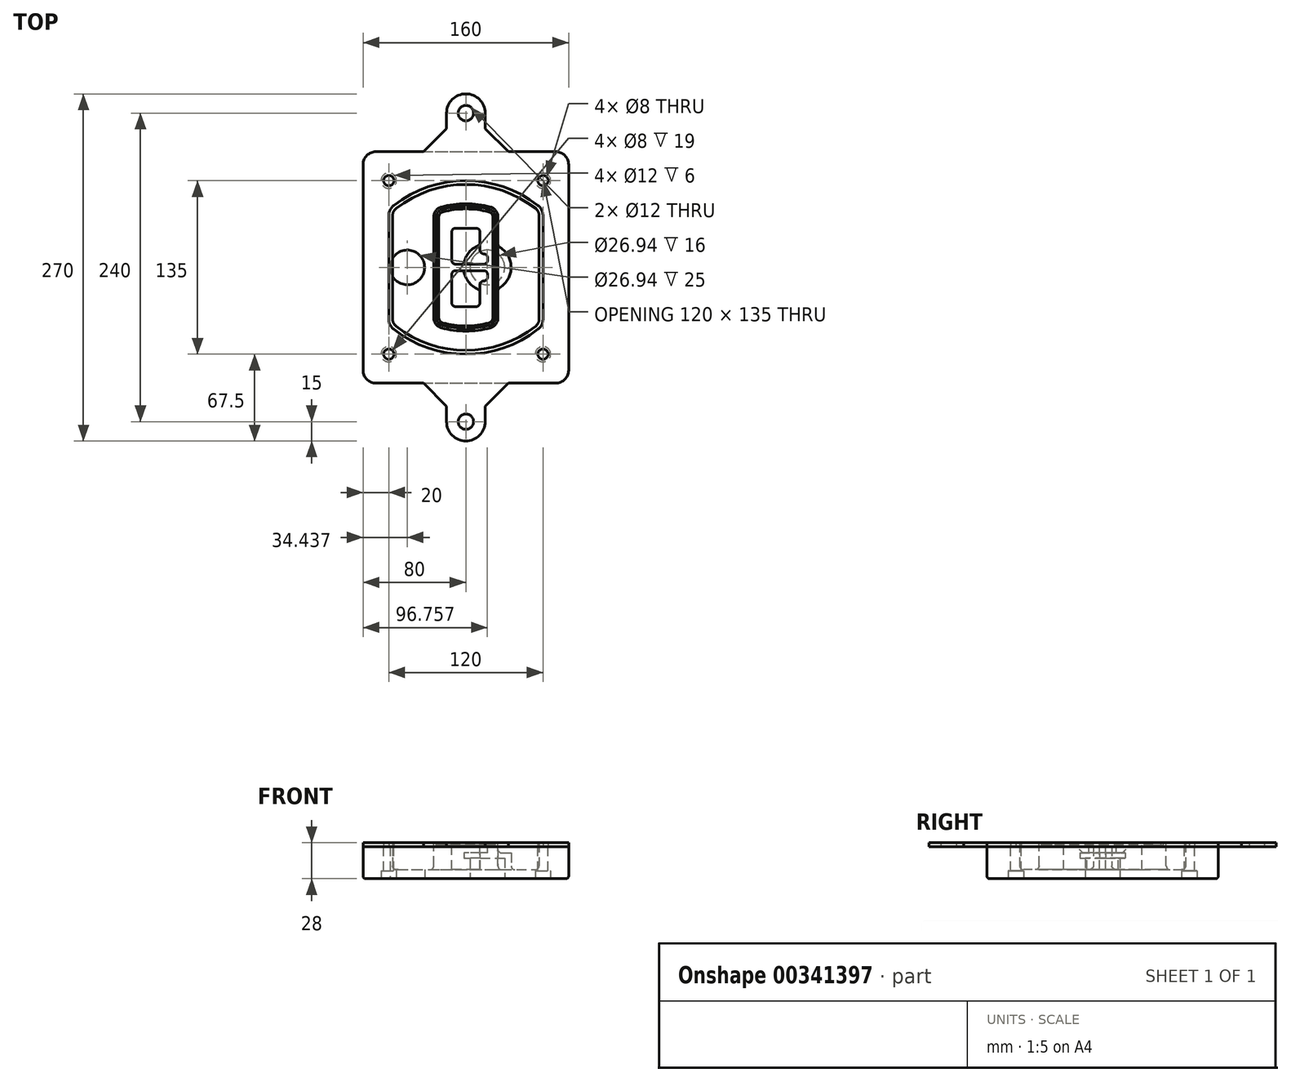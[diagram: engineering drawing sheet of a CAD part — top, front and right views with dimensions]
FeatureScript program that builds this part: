
annotation { "Feature Type Name" : "Feature", "Feature Type Description" : "" }
export const myFeature = defineFeature(function(context is Context, id is Id, definition is map)
    precondition{}
    {
        {
            var Q0;
            Q0=qCreatedBy(makeId("Top.planeOp"),FACE);
            var sketch = newSketch(context, id + "F0", { "sketchPlane" : qUnion([Q0])});
            skPoint(sketch, "E0.rect.middle", {"position": v(0, 0) * mm});
            skLineSegment(sketch, "E1.bottom", {"start": v(-70, -90) * mm, "end": v(70, -90) * mm});
            skLineSegment(sketch, "E1.top", {"start": v(-70, 90) * mm, "end": v(70, 90) * mm});
            skLineSegment(sketch, "E1.left", {"start": v(-80, -80) * mm, "end": v(-80, 80) * mm});
            skLineSegment(sketch, "E1.right", {"start": v(80, -80) * mm, "end": v(80, 80) * mm});
            skLineSegment(sketch, "E2", {"start": v(-80, 90) * mm, "end": v(80, -90) * mm, "construction": true});
            skLineSegment(sketch, "E3", {"start": v(80, 90) * mm, "end": v(-80, -90) * mm, "construction": true});
            skCircle(sketch, "E4", {"center": v(-60, 67.5) * mm, "radius": 4 * mm});
            skCircle(sketch, "E5", {"center": v(60, 67.5) * mm, "radius": 4 * mm});
            skCircle(sketch, "E6", {"center": v(60, -67.5) * mm, "radius": 4 * mm});
            skCircle(sketch, "E7", {"center": v(-60, -67.5) * mm, "radius": 4 * mm});
            skLineSegment(sketch, "E8", {"start": v(-60, 67.5) * mm, "end": v(60, 67.5) * mm, "construction": true});
            skLineSegment(sketch, "E9", {"start": v(60, 67.5) * mm, "end": v(60, -67.5) * mm, "construction": true});
            skLineSegment(sketch, "E10", {"start": v(60, -67.5) * mm, "end": v(-60, -67.5) * mm, "construction": true});
            skLineSegment(sketch, "E11", {"start": v(-60, -67.5) * mm, "end": v(-60, 67.5) * mm, "construction": true});
            skLineSegment(sketch, "E12", {"start": v(-60, 40.3) * mm, "end": v(-60, -40.3) * mm});
            skLineSegment(sketch, "E13", {"start": v(60, 40.3) * mm, "end": v(60, -40.3) * mm});
            skArc(sketch, "E14", {"start": v(56.15, 48.18) * mm, "mid": v(0, 67.5) * mm, "end": v(-56.15, 48.18) * mm});
            skArc(sketch, "E15", {"start": v(-56.15, -48.18) * mm, "mid": v(0, -67.5) * mm, "end": v(56.15, -48.18) * mm});
            skLineSegment(sketch, "E16", {"start": v(-60, 0) * mm, "end": v(60, 0) * mm, "construction": true});
            skPoint(sketch, "E17.visualSharp", {"position": v(-60, -45) * mm});
            skArc(sketch, "E17.filletArc", {"start": v(-60, -40.3) * mm, "mid": v(-58.99, -44.68) * mm, "end": v(-56.15, -48.18) * mm});
            skPoint(sketch, "E18.visualSharp", {"position": v(-60, 45) * mm});
            skArc(sketch, "E18.filletArc", {"start": v(-56.15, 48.18) * mm, "mid": v(-58.99, 44.68) * mm, "end": v(-60, 40.3) * mm});
            skPoint(sketch, "E19.visualSharp", {"position": v(60, 45) * mm});
            skArc(sketch, "E19.filletArc", {"start": v(60, 40.3) * mm, "mid": v(58.99, 44.68) * mm, "end": v(56.15, 48.18) * mm});
            skPoint(sketch, "E20.visualSharp", {"position": v(60, -45) * mm});
            skArc(sketch, "E20.filletArc", {"start": v(56.15, -48.18) * mm, "mid": v(58.99, -44.68) * mm, "end": v(60, -40.3) * mm});
            skPoint(sketch, "E21.visualSharp", {"position": v(-80, 90) * mm});
            skArc(sketch, "E21.filletArc", {"start": v(-70, 90) * mm, "mid": v(-77.07, 87.07) * mm, "end": v(-80, 80) * mm});
            skPoint(sketch, "E22.visualSharp", {"position": v(80, 90) * mm});
            skArc(sketch, "E22.filletArc", {"start": v(80, 80) * mm, "mid": v(77.07, 87.07) * mm, "end": v(70, 90) * mm});
            skPoint(sketch, "E23.visualSharp", {"position": v(80, -90) * mm});
            skArc(sketch, "E23.filletArc", {"start": v(70, -90) * mm, "mid": v(77.07, -87.07) * mm, "end": v(80, -80) * mm});
            skPoint(sketch, "E24.visualSharp", {"position": v(-80, -90) * mm});
            skArc(sketch, "E24.filletArc", {"start": v(-80, -80) * mm, "mid": v(-77.07, -87.07) * mm, "end": v(-70, -90) * mm});
            skArc(sketch, "E25.0", {"start": v(57, 40.3) * mm, "mid": v(56.3, 43.36) * mm, "end": v(54.3, 45.81) * mm});
            skLineSegment(sketch, "E25.1", {"start": v(57, 40.3) * mm, "end": v(57, -40.3) * mm});
            skArc(sketch, "E25.2", {"start": v(54.3, -45.81) * mm, "mid": v(56.3, -43.36) * mm, "end": v(57, -40.3) * mm});
            skArc(sketch, "E25.3", {"start": v(-54.3, -45.81) * mm, "mid": v(0, -64.5) * mm, "end": v(54.3, -45.81) * mm});
            skArc(sketch, "E25.4", {"start": v(-57, -40.3) * mm, "mid": v(-56.3, -43.36) * mm, "end": v(-54.3, -45.81) * mm});
            skArc(sketch, "E25.5", {"start": v(54.3, 45.81) * mm, "mid": v(0, 64.5) * mm, "end": v(-54.3, 45.81) * mm});
            skLineSegment(sketch, "E25.6", {"start": v(-57, 40.3) * mm, "end": v(-57, -40.3) * mm});
            skArc(sketch, "E25.7", {"start": v(-54.3, 45.81) * mm, "mid": v(-56.3, 43.36) * mm, "end": v(-57, 40.3) * mm});
            skArc(sketch, "E26.0", {"start": v(-58.62, 51.33) * mm, "mid": v(-62.58, 46.43) * mm, "end": v(-64, 40.3) * mm});
            skArc(sketch, "E26.1", {"start": v(58.62, 51.33) * mm, "mid": v(0, 71.5) * mm, "end": v(-58.62, 51.33) * mm});
            skArc(sketch, "E26.2", {"start": v(64, 40.3) * mm, "mid": v(62.58, 46.43) * mm, "end": v(58.62, 51.33) * mm});
            skLineSegment(sketch, "E26.3", {"start": v(64, 40.3) * mm, "end": v(64, -40.3) * mm});
            skArc(sketch, "E26.4", {"start": v(58.62, -51.33) * mm, "mid": v(62.58, -46.43) * mm, "end": v(64, -40.3) * mm});
            skLineSegment(sketch, "E26.5", {"start": v(-64, 40.3) * mm, "end": v(-64, -40.3) * mm});
            skArc(sketch, "E26.6", {"start": v(-58.62, -51.33) * mm, "mid": v(0, -71.5) * mm, "end": v(58.62, -51.33) * mm});
            skArc(sketch, "E26.7", {"start": v(-64, -40.3) * mm, "mid": v(-62.58, -46.43) * mm, "end": v(-58.62, -51.33) * mm});
            skSolve(sketch);
        }
        {
            var Q0;
            Q0=makeQuery(id+"F0.imprint","IMPRINT",FACE,{"disambiguationData":[TD([[makeQuery(id+"F0.imprint","IMPRINT",EDGE,{"derivedFrom":sQuery(id+"F0.wireOp",EDGE,"E1.bottom")}),1.0]])]});
            var Q1;
            Q1=makeQuery(id+"F0.imprint","IMPRINT",FACE,{"disambiguationData":[TD([[makeQuery(id+"F0.imprint","IMPRINT",EDGE,{"derivedFrom":sQuery(id+"F0.wireOp",EDGE,"E12")}),1.0]])]});
            var Q2;
            Q2=makeQuery(id+"F0.imprint","IMPRINT",FACE,{"disambiguationData":[TD([[makeQuery(id+"F0.imprint","IMPRINT",EDGE,{"derivedFrom":sQuery(id+"F0.wireOp",EDGE,"E25.0")}),1.0]])]});
            var Q3;
            Q3=makeQuery(id+"F0.imprint","IMPRINT",FACE,{"disambiguationData":[TD([[makeQuery(id+"F0.imprint","IMPRINT",EDGE,{"derivedFrom":sQuery(id+"F0.wireOp",EDGE,"E12")}),-1.0]])]});
            extrude(context, id + "F1", {"entities" : qUnion([Q0, Q1, Q2, Q3]), "oppositeDirection" : true, "depth" : 25 * mm});
        }
        {
            var Q0;
            Q0=makeQuery(id+"F0.imprint","IMPRINT",FACE,{"disambiguationData":[TD([[makeQuery(id+"F0.imprint","IMPRINT",EDGE,{"derivedFrom":sQuery(id+"F0.wireOp",EDGE,"E12")}),1.0]])]});
            extrude(context, id + "F2", {"entities" : qUnion([Q0]), "operationType" : NewBodyOperationType.ADD, "depth" : 3 * mm});
        }
        {
            var Q0;
            Q0=makeQuery(id+"F0.imprint","IMPRINT",FACE,{"disambiguationData":[TD([[makeQuery(id+"F0.imprint","IMPRINT",EDGE,{"derivedFrom":sQuery(id+"F0.wireOp",EDGE,"E25.0")}),1.0]])]});
            extrude(context, id + "F3", {"entities" : qUnion([Q0]), "operationType" : NewBodyOperationType.REMOVE, "oppositeDirection" : true, "depth" : 18 * mm});
        }
        {
            var Q0;
            Q0=makeQuery(id+"F2.opExtrude","CAP_FACE",FACE,{"disambiguationData":[OSD([sQuery(id+"F0.wireOp",EDGE,"E12"),sQuery(id+"F0.wireOp",EDGE,"E13"),sQuery(id+"F0.wireOp",EDGE,"E14"),sQuery(id+"F0.wireOp",EDGE,"E15"),sQuery(id+"F0.wireOp",EDGE,"E17.filletArc"),sQuery(id+"F0.wireOp",EDGE,"E18.filletArc"),sQuery(id+"F0.wireOp",EDGE,"E19.filletArc"),sQuery(id+"F0.wireOp",EDGE,"E20.filletArc"),sQuery(id+"F0.wireOp",EDGE,"E25.0"),sQuery(id+"F0.wireOp",EDGE,"E25.1"),sQuery(id+"F0.wireOp",EDGE,"E25.2"),sQuery(id+"F0.wireOp",EDGE,"E25.3"),sQuery(id+"F0.wireOp",EDGE,"E25.4"),sQuery(id+"F0.wireOp",EDGE,"E25.5"),sQuery(id+"F0.wireOp",EDGE,"E25.6"),sQuery(id+"F0.wireOp",EDGE,"E25.7")])],"isStart":false});
            var sketch = newSketch(context, id + "F4", { "sketchPlane" : qUnion([Q0])});
            skArc(sketch, "E27.0", {"start": v(-19.08, -46.97) * mm, "mid": v(0, -49.5) * mm, "end": v(19.08, -46.97) * mm});
            skArc(sketch, "E28.0", {"start": v(19.08, 46.97) * mm, "mid": v(0, 49.5) * mm, "end": v(-19.08, 46.97) * mm});
            skLineSegment(sketch, "E29", {"start": v(-25, 39.25) * mm, "end": v(-25, -39.25) * mm});
            skLineSegment(sketch, "E30", {"start": v(25, 39.25) * mm, "end": v(25, -39.25) * mm});
            skLineSegment(sketch, "E31", {"start": v(-25, 45.1) * mm, "end": v(25, 45.1) * mm, "construction": true});
            skLineSegment(sketch, "E32", {"start": v(-25, -45.1) * mm, "end": v(25, -45.1) * mm, "construction": true});
            skPoint(sketch, "E33.visualSharp", {"position": v(-25, 45.1) * mm});
            skArc(sketch, "E33.filletArc", {"start": v(-19.08, 46.97) * mm, "mid": v(-23.35, 44.11) * mm, "end": v(-25, 39.25) * mm});
            skPoint(sketch, "E34.visualSharp", {"position": v(25, 45.1) * mm});
            skArc(sketch, "E34.filletArc", {"start": v(25, 39.25) * mm, "mid": v(23.35, 44.11) * mm, "end": v(19.08, 46.97) * mm});
            skPoint(sketch, "E35.visualSharp", {"position": v(25, -45.1) * mm});
            skArc(sketch, "E35.filletArc", {"start": v(19.08, -46.97) * mm, "mid": v(23.35, -44.11) * mm, "end": v(25, -39.25) * mm});
            skPoint(sketch, "E36.visualSharp", {"position": v(-25, -45.1) * mm});
            skArc(sketch, "E36.filletArc", {"start": v(-25, -39.25) * mm, "mid": v(-23.35, -44.11) * mm, "end": v(-19.08, -46.97) * mm});
            skArc(sketch, "E37.0", {"start": v(54.3, 45.81) * mm, "mid": v(0, 64.5) * mm, "end": v(-54.3, 45.81) * mm});
            skArc(sketch, "E37.1", {"start": v(-54.3, 45.81) * mm, "mid": v(-56.3, 43.36) * mm, "end": v(-57, 40.3) * mm});
            skLineSegment(sketch, "E37.2", {"start": v(-57, 40.3) * mm, "end": v(-57, -40.3) * mm});
            skArc(sketch, "E37.3", {"start": v(-57, -40.3) * mm, "mid": v(-56.3, -43.36) * mm, "end": v(-54.3, -45.81) * mm});
            skArc(sketch, "E37.4", {"start": v(-54.3, -45.81) * mm, "mid": v(0, -64.5) * mm, "end": v(54.3, -45.81) * mm});
            skArc(sketch, "E37.5", {"start": v(54.3, -45.81) * mm, "mid": v(56.3, -43.36) * mm, "end": v(57, -40.3) * mm});
            skLineSegment(sketch, "E37.6", {"start": v(57, 40.3) * mm, "end": v(57, -40.3) * mm});
            skArc(sketch, "E37.7", {"start": v(57, 40.3) * mm, "mid": v(56.3, 43.36) * mm, "end": v(54.3, 45.81) * mm});
            skLineSegment(sketch, "E38.0", {"start": v(23, 39.25) * mm, "end": v(23, -39.25) * mm});
            skArc(sketch, "E38.1", {"start": v(18.56, -45.04) * mm, "mid": v(21.76, -42.9) * mm, "end": v(23, -39.25) * mm});
            skArc(sketch, "E38.2", {"start": v(-18.56, -45.04) * mm, "mid": v(0, -47.5) * mm, "end": v(18.56, -45.04) * mm});
            skArc(sketch, "E38.3", {"start": v(-23, -39.25) * mm, "mid": v(-21.76, -42.9) * mm, "end": v(-18.56, -45.04) * mm});
            skLineSegment(sketch, "E38.4", {"start": v(-23, 39.25) * mm, "end": v(-23, -39.25) * mm});
            skArc(sketch, "E38.5", {"start": v(23, 39.25) * mm, "mid": v(21.76, 42.9) * mm, "end": v(18.56, 45.04) * mm});
            skArc(sketch, "E38.6", {"start": v(-18.56, 45.04) * mm, "mid": v(-21.76, 42.9) * mm, "end": v(-23, 39.25) * mm});
            skArc(sketch, "E38.7", {"start": v(18.56, 45.04) * mm, "mid": v(0, 47.5) * mm, "end": v(-18.56, 45.04) * mm});
            skArc(sketch, "E39.0", {"start": v(21, 39.25) * mm, "mid": v(20.18, 41.68) * mm, "end": v(18.04, 43.1) * mm});
            skLineSegment(sketch, "E39.1", {"start": v(21, 39.25) * mm, "end": v(21, -39.25) * mm});
            skArc(sketch, "E39.2", {"start": v(18.04, -43.1) * mm, "mid": v(20.18, -41.68) * mm, "end": v(21, -39.25) * mm});
            skArc(sketch, "E39.3", {"start": v(-18.04, -43.1) * mm, "mid": v(0, -45.5) * mm, "end": v(18.04, -43.1) * mm});
            skArc(sketch, "E39.4", {"start": v(-21, -39.25) * mm, "mid": v(-20.18, -41.68) * mm, "end": v(-18.04, -43.1) * mm});
            skArc(sketch, "E39.5", {"start": v(18.04, 43.1) * mm, "mid": v(0, 45.5) * mm, "end": v(-18.04, 43.1) * mm});
            skLineSegment(sketch, "E39.6", {"start": v(-21, 39.25) * mm, "end": v(-21, -39.25) * mm});
            skArc(sketch, "E39.7", {"start": v(-18.04, 43.1) * mm, "mid": v(-20.18, 41.68) * mm, "end": v(-21, 39.25) * mm});
            skLineSegment(sketch, "E40", {"start": v(-25, 0) * mm, "end": v(25, 0) * mm, "construction": true});
            skLineSegment(sketch, "E41", {"start": v(-11, 5.5) * mm, "end": v(-11, 27.5) * mm});
            skLineSegment(sketch, "E42", {"start": v(-8, 30.5) * mm, "end": v(8, 30.5) * mm});
            skLineSegment(sketch, "E43", {"start": v(11, 27.5) * mm, "end": v(11, 13.5) * mm});
            skLineSegment(sketch, "E44", {"start": v(14, 10.5) * mm, "end": v(14, 10.5) * mm});
            skLineSegment(sketch, "E45", {"start": v(17, 7.5) * mm, "end": v(17, 5.5) * mm});
            skLineSegment(sketch, "E46", {"start": v(14, 2.5) * mm, "end": v(-8, 2.5) * mm});
            skPoint(sketch, "E47.visualSharp", {"position": v(-11, 30.5) * mm});
            skArc(sketch, "E47.filletArc", {"start": v(-8, 30.5) * mm, "mid": v(-10.12, 29.62) * mm, "end": v(-11, 27.5) * mm});
            skPoint(sketch, "E48.visualSharp", {"position": v(11, 30.5) * mm});
            skArc(sketch, "E48.filletArc", {"start": v(11, 27.5) * mm, "mid": v(10.12, 29.62) * mm, "end": v(8, 30.5) * mm});
            skPoint(sketch, "E49.visualSharp", {"position": v(11, 10.5) * mm});
            skArc(sketch, "E49.filletArc", {"start": v(11, 13.5) * mm, "mid": v(11.88, 11.38) * mm, "end": v(14, 10.5) * mm});
            skPoint(sketch, "E50.visualSharp", {"position": v(17, 10.5) * mm});
            skArc(sketch, "E50.filletArc", {"start": v(17, 7.5) * mm, "mid": v(16.12, 9.62) * mm, "end": v(14, 10.5) * mm});
            skPoint(sketch, "E51.visualSharp", {"position": v(17, 2.5) * mm});
            skArc(sketch, "E51.filletArc", {"start": v(14, 2.5) * mm, "mid": v(16.12, 3.38) * mm, "end": v(17, 5.5) * mm});
            skPoint(sketch, "E52.visualSharp", {"position": v(-11, 2.5) * mm});
            skArc(sketch, "E52.filletArc", {"start": v(-11, 5.5) * mm, "mid": v(-10.12, 3.38) * mm, "end": v(-8, 2.5) * mm});
            skLineSegment(sketch, "E53.0.MirrorCS", {"start": v(14, -2.5) * mm, "end": v(-8, -2.5) * mm});
            skArc(sketch, "E54.0.MirrorCS", {"start": v(-11, -5.5) * mm, "mid": v(-10.12, -3.38) * mm, "end": v(-8, -2.5) * mm});
            skLineSegment(sketch, "E55.0.MirrorCS", {"start": v(-11, -5.5) * mm, "end": v(-11, -27.5) * mm});
            skArc(sketch, "E56.0.MirrorCS", {"start": v(-8, -30.5) * mm, "mid": v(-10.12, -29.62) * mm, "end": v(-11, -27.5) * mm});
            skLineSegment(sketch, "E57.0.MirrorCS", {"start": v(-8, -30.5) * mm, "end": v(8, -30.5) * mm});
            skArc(sketch, "E58.0.MirrorCS", {"start": v(11, -27.5) * mm, "mid": v(10.12, -29.62) * mm, "end": v(8, -30.5) * mm});
            skLineSegment(sketch, "E59.0.MirrorCS", {"start": v(11, -27.5) * mm, "end": v(11, -13.5) * mm});
            skArc(sketch, "E60.0.MirrorCS", {"start": v(11, -13.5) * mm, "mid": v(11.88, -11.38) * mm, "end": v(14, -10.5) * mm});
            skArc(sketch, "E61.0.MirrorCS", {"start": v(17, -7.5) * mm, "mid": v(16.12, -9.62) * mm, "end": v(14, -10.5) * mm});
            skLineSegment(sketch, "E62.0.MirrorCS", {"start": v(17, -7.5) * mm, "end": v(17, -5.5) * mm});
            skArc(sketch, "E63.0.MirrorCS", {"start": v(14, -2.5) * mm, "mid": v(16.12, -3.38) * mm, "end": v(17, -5.5) * mm});
            skSolve(sketch);
        }
        {
            var Q0;
            Q0=makeQuery(id+"F4.imprint","IMPRINT",FACE,{"disambiguationData":[TD([[makeQuery(id+"F4.imprint","IMPRINT",EDGE,{"derivedFrom":sQuery(id+"F4.wireOp",EDGE,"E27.0")}),1.0]])]});
            var Q1;
            Q1=makeQuery(id+"F4.imprint","IMPRINT",FACE,{"disambiguationData":[TD([[makeQuery(id+"F4.imprint","IMPRINT",EDGE,{"derivedFrom":sQuery(id+"F4.wireOp",EDGE,"E38.0")}),-1.0]])]});
            var Q2;
            Q2=makeQuery(id+"F4.imprint","IMPRINT",FACE,{"disambiguationData":[TD([[makeQuery(id+"F4.imprint","IMPRINT",EDGE,{"derivedFrom":sQuery(id+"F4.wireOp",EDGE,"E39.0")}),1.0]])]});
            extrude(context, id + "F5", {"entities" : qUnion([Q0, Q1, Q2]), "operationType" : NewBodyOperationType.ADD, "endBound" : BoundingType.UP_TO_NEXT, "oppositeDirection" : true, "depth" : 25 * mm});
        }
        {
            var Q0;
            Q0=makeQuery(id+"F4.imprint","IMPRINT",FACE,{"disambiguationData":[TD([[makeQuery(id+"F4.imprint","IMPRINT",EDGE,{"derivedFrom":sQuery(id+"F4.wireOp",EDGE,"E38.0")}),-1.0]])]});
            extrude(context, id + "F6", {"entities" : qUnion([Q0]), "operationType" : NewBodyOperationType.REMOVE, "oppositeDirection" : true, "depth" : 2 * mm});
        }
        {
            var Q0;
            Q0=makeQuery(id+"F1.opExtrude","CAP_FACE",FACE,{"disambiguationData":[OSD([sQuery(id+"F0.wireOp",EDGE,"E1.bottom"),sQuery(id+"F0.wireOp",EDGE,"E1.top"),sQuery(id+"F0.wireOp",EDGE,"E1.left"),sQuery(id+"F0.wireOp",EDGE,"E1.right"),sQuery(id+"F0.wireOp",EDGE,"E4"),sQuery(id+"F0.wireOp",EDGE,"E5"),sQuery(id+"F0.wireOp",EDGE,"E6"),sQuery(id+"F0.wireOp",EDGE,"E7"),sQuery(id+"F0.wireOp",EDGE,"E21.filletArc"),sQuery(id+"F0.wireOp",EDGE,"E22.filletArc"),sQuery(id+"F0.wireOp",EDGE,"E23.filletArc"),sQuery(id+"F0.wireOp",EDGE,"E24.filletArc")])],"isStart":false});
            var sketch = newSketch(context, id + "F7", { "sketchPlane" : qUnion([Q0])});
            skCircle(sketch, "E64", {"center": v(16.76, 0) * mm, "radius": 13.47 * mm});
            skCircle(sketch, "E65", {"center": v(-45.56, 0) * mm, "radius": 13.47 * mm});
            skLineSegment(sketch, "E66", {"start": v(80, 0) * mm, "end": v(-80, 0) * mm});
            skCircle(sketch, "E67", {"center": v(16.76, 0) * mm, "radius": 18.47 * mm});
            skCircle(sketch, "E68", {"center": v(60, -67.5) * mm, "radius": 6 * mm});
            skCircle(sketch, "E69", {"center": v(-60, -67.5) * mm, "radius": 6 * mm});
            skCircle(sketch, "E70", {"center": v(-60, 67.5) * mm, "radius": 6 * mm});
            skCircle(sketch, "E71", {"center": v(60, 67.5) * mm, "radius": 6 * mm});
            skSolve(sketch);
        }
        {
            var Q0;
            {var subQ1=sQuery(id+"F7.wireOp",EDGE,"E66");var subQ4=sQuery(id+"F7.wireOp",EDGE,"E64");var subQ6=makeQuery(id+"F7.imprint","INTERSECT",VERTEX,{"disambiguationData":[OD(0.0)],"derivedFrom":[subQ4,subQ1]});Q0=makeQuery(id+"F7.imprint","IMPRINT",FACE,{"disambiguationData":[TD([[makeQuery(id+"F7.imprint","IMPRINT",EDGE,{"disambiguationData":[TD([[subQ6,-1.0]])],"derivedFrom":subQ4}),-1.0]])]});}
            var Q1;
            {var subQ0=sQuery(id+"F7.wireOp",EDGE,"E66");var subQ1=sQuery(id+"F7.wireOp",EDGE,"E64");var subQ3=makeQuery(id+"F7.imprint","INTERSECT",VERTEX,{"disambiguationData":[OD(0.0)],"derivedFrom":[subQ1,subQ0]});Q1=makeQuery(id+"F7.imprint","IMPRINT",FACE,{"disambiguationData":[TD([[makeQuery(id+"F7.imprint","IMPRINT",EDGE,{"disambiguationData":[TD([[subQ3,-1.0]])],"derivedFrom":subQ1}),1.0]])]});}
            var Q2;
            {var subQ0=sQuery(id+"F7.wireOp",EDGE,"E66");var subQ1=sQuery(id+"F7.wireOp",EDGE,"E64");var subQ3=makeQuery(id+"F7.imprint","INTERSECT",VERTEX,{"disambiguationData":[OD(0.0)],"derivedFrom":[subQ1,subQ0]});Q2=makeQuery(id+"F7.imprint","IMPRINT",FACE,{"disambiguationData":[TD([[makeQuery(id+"F7.imprint","IMPRINT",EDGE,{"disambiguationData":[TD([[subQ3,1.0]])],"derivedFrom":subQ1}),1.0]])]});}
            var Q3;
            {var subQ1=sQuery(id+"F7.wireOp",EDGE,"E66");var subQ4=sQuery(id+"F7.wireOp",EDGE,"E64");var subQ6=makeQuery(id+"F7.imprint","INTERSECT",VERTEX,{"disambiguationData":[OD(0.0)],"derivedFrom":[subQ4,subQ1]});Q3=makeQuery(id+"F7.imprint","IMPRINT",FACE,{"disambiguationData":[TD([[makeQuery(id+"F7.imprint","IMPRINT",EDGE,{"disambiguationData":[TD([[subQ6,1.0]])],"derivedFrom":subQ4}),-1.0]])]});}
            extrude(context, id + "F8", {"entities" : qUnion([Q0, Q1, Q2, Q3]), "operationType" : NewBodyOperationType.ADD, "oppositeDirection" : true, "depth" : 20 * mm});
        }
        {
            var Q0;
            {var subQ0=sQuery(id+"F7.wireOp",EDGE,"E66");var subQ1=sQuery(id+"F7.wireOp",EDGE,"E64");var subQ3=makeQuery(id+"F7.imprint","INTERSECT",VERTEX,{"disambiguationData":[OD(0.0)],"derivedFrom":[subQ1,subQ0]});Q0=makeQuery(id+"F7.imprint","IMPRINT",FACE,{"disambiguationData":[TD([[makeQuery(id+"F7.imprint","IMPRINT",EDGE,{"disambiguationData":[TD([[subQ3,-1.0]])],"derivedFrom":subQ1}),1.0]])]});}
            var Q1;
            {var subQ0=sQuery(id+"F7.wireOp",EDGE,"E66");var subQ1=sQuery(id+"F7.wireOp",EDGE,"E64");var subQ3=makeQuery(id+"F7.imprint","INTERSECT",VERTEX,{"disambiguationData":[OD(0.0)],"derivedFrom":[subQ1,subQ0]});Q1=makeQuery(id+"F7.imprint","IMPRINT",FACE,{"disambiguationData":[TD([[makeQuery(id+"F7.imprint","IMPRINT",EDGE,{"disambiguationData":[TD([[subQ3,1.0]])],"derivedFrom":subQ1}),1.0]])]});}
            extrude(context, id + "F9", {"entities" : qUnion([Q0, Q1]), "operationType" : NewBodyOperationType.REMOVE, "oppositeDirection" : true, "depth" : 16 * mm});
        }
        {
            var Q0;
            {var subQ0=sQuery(id+"F7.wireOp",EDGE,"E66");var subQ1=sQuery(id+"F7.wireOp",EDGE,"E65");var subQ3=makeQuery(id+"F7.imprint","INTERSECT",VERTEX,{"disambiguationData":[OD(0.0)],"derivedFrom":[subQ1,subQ0]});Q0=makeQuery(id+"F7.imprint","IMPRINT",FACE,{"disambiguationData":[TD([[makeQuery(id+"F7.imprint","IMPRINT",EDGE,{"disambiguationData":[TD([[subQ3,-1.0]])],"derivedFrom":subQ1}),1.0]])]});}
            var Q1;
            {var subQ0=sQuery(id+"F7.wireOp",EDGE,"E66");var subQ1=sQuery(id+"F7.wireOp",EDGE,"E65");var subQ3=makeQuery(id+"F7.imprint","INTERSECT",VERTEX,{"disambiguationData":[OD(0.0)],"derivedFrom":[subQ1,subQ0]});Q1=makeQuery(id+"F7.imprint","IMPRINT",FACE,{"disambiguationData":[TD([[makeQuery(id+"F7.imprint","IMPRINT",EDGE,{"disambiguationData":[TD([[subQ3,1.0]])],"derivedFrom":subQ1}),1.0]])]});}
            extrude(context, id + "F10", {"entities" : qUnion([Q0, Q1]), "operationType" : NewBodyOperationType.REMOVE, "oppositeDirection" : true, "depth" : 25 * mm});
        }
        {
            var Q0;
            Q0=makeQuery(id+"F7.imprint","IMPRINT",FACE,{"disambiguationData":[TD([[makeQuery(id+"F7.imprint","IMPRINT",EDGE,{"derivedFrom":sQuery(id+"F7.wireOp",EDGE,"E68")}),1.0]])]});
            var Q1;
            Q1=makeQuery(id+"F7.imprint","IMPRINT",FACE,{"disambiguationData":[TD([[makeQuery(id+"F7.imprint","IMPRINT",EDGE,{"derivedFrom":makeQuery(id+"F1.opExtrude","CAP_EDGE",EDGE,{"disambiguationData":[OSD([sQuery(id+"F0.wireOp",EDGE,"E5")])],"isStart":false})}),-1.0]])]});
            var Q2;
            Q2=makeQuery(id+"F7.imprint","IMPRINT",FACE,{"disambiguationData":[TD([[makeQuery(id+"F7.imprint","IMPRINT",EDGE,{"derivedFrom":sQuery(id+"F7.wireOp",EDGE,"E69")}),1.0]])]});
            var Q3;
            Q3=makeQuery(id+"F7.imprint","IMPRINT",FACE,{"disambiguationData":[TD([[makeQuery(id+"F7.imprint","IMPRINT",EDGE,{"derivedFrom":makeQuery(id+"F1.opExtrude","CAP_EDGE",EDGE,{"disambiguationData":[OSD([sQuery(id+"F0.wireOp",EDGE,"E4")])],"isStart":false})}),-1.0]])]});
            var Q4;
            Q4=makeQuery(id+"F7.imprint","IMPRINT",FACE,{"disambiguationData":[TD([[makeQuery(id+"F7.imprint","IMPRINT",EDGE,{"derivedFrom":sQuery(id+"F7.wireOp",EDGE,"E70")}),1.0]])]});
            var Q5;
            Q5=makeQuery(id+"F7.imprint","IMPRINT",FACE,{"disambiguationData":[TD([[makeQuery(id+"F7.imprint","IMPRINT",EDGE,{"derivedFrom":makeQuery(id+"F1.opExtrude","CAP_EDGE",EDGE,{"disambiguationData":[OSD([sQuery(id+"F0.wireOp",EDGE,"E7")])],"isStart":false})}),-1.0]])]});
            var Q6;
            Q6=makeQuery(id+"F7.imprint","IMPRINT",FACE,{"disambiguationData":[TD([[makeQuery(id+"F7.imprint","IMPRINT",EDGE,{"derivedFrom":sQuery(id+"F7.wireOp",EDGE,"E71")}),1.0]])]});
            var Q7;
            Q7=makeQuery(id+"F7.imprint","IMPRINT",FACE,{"disambiguationData":[TD([[makeQuery(id+"F7.imprint","IMPRINT",EDGE,{"derivedFrom":makeQuery(id+"F1.opExtrude","CAP_EDGE",EDGE,{"disambiguationData":[OSD([sQuery(id+"F0.wireOp",EDGE,"E6")])],"isStart":false})}),-1.0]])]});
            extrude(context, id + "F11", {"entities" : qUnion([Q0, Q1, Q2, Q3, Q4, Q5, Q6, Q7]), "operationType" : NewBodyOperationType.REMOVE, "oppositeDirection" : true, "depth" : 6 * mm});
        }
        {
            var Q0;
            Q0=makeQuery(id+"F9.boolean.opBoolean","COPY",FACE,{"derivedFrom":makeQuery(id+"F9.opExtrude","CAP_FACE",FACE,{"disambiguationData":[OSD([sQuery(id+"F7.wireOp",EDGE,"E64")])],"isStart":false})});
            var sketch = newSketch(context, id + "F12", { "sketchPlane" : qUnion([Q0])});
            skArc(sketch, "E72.0", {"start": v(11, 17.55) * mm, "mid": v(2.57, 11.82) * mm, "end": v(-1.54, 2.5) * mm});
            skArc(sketch, "E72.1", {"start": v(-1.54, -2.5) * mm, "mid": v(2.57, -11.82) * mm, "end": v(11, -17.55) * mm});
            skLineSegment(sketch, "E73", {"start": v(-1.54, -2.5) * mm, "end": v(14, -2.5) * mm});
            skLineSegment(sketch, "E74.0", {"start": v(14, 2.5) * mm, "end": v(-1.54, 2.5) * mm});
            skArc(sketch, "E74.1", {"start": v(14, 2.5) * mm, "mid": v(16.12, 3.38) * mm, "end": v(17, 5.5) * mm});
            skLineSegment(sketch, "E74.2", {"start": v(17, 7.5) * mm, "end": v(17, 5.5) * mm});
            skArc(sketch, "E74.3", {"start": v(17, 7.5) * mm, "mid": v(16.12, 9.62) * mm, "end": v(14, 10.5) * mm});
            skArc(sketch, "E74.4", {"start": v(11, 13.5) * mm, "mid": v(11.88, 11.38) * mm, "end": v(14, 10.5) * mm});
            skLineSegment(sketch, "E74.5", {"start": v(11, 17.55) * mm, "end": v(11, 13.5) * mm});
            skLineSegment(sketch, "E74.7", {"start": v(14, -2.5) * mm, "end": v(-1.54, -2.5) * mm});
            skArc(sketch, "E74.8", {"start": v(14, -2.5) * mm, "mid": v(16.12, -3.38) * mm, "end": v(17, -5.5) * mm});
            skLineSegment(sketch, "E74.9", {"start": v(17, -7.5) * mm, "end": v(17, -5.5) * mm});
            skArc(sketch, "E74.10", {"start": v(17, -7.5) * mm, "mid": v(16.12, -9.62) * mm, "end": v(14, -10.5) * mm});
            skArc(sketch, "E74.11", {"start": v(11, -13.5) * mm, "mid": v(11.88, -11.38) * mm, "end": v(14, -10.5) * mm});
            skLineSegment(sketch, "E74.12", {"start": v(11, -17.55) * mm, "end": v(11, -13.5) * mm});
            skPoint(sketch, "E75.orphan", {"position": v(11, -27.5) * mm});
            skPoint(sketch, "E76.orphan", {"position": v(-8, -2.5) * mm});
            skPoint(sketch, "E77.orphan", {"position": v(-8, 2.5) * mm});
            skPoint(sketch, "E78.orphan", {"position": v(11, 27.5) * mm});
            skSolve(sketch);
        }
        {
            var Q0;
            {var subQ7=sQuery(id+"F12.wireOp",EDGE,"E72.0");var subQ14=sQuery(id+"F12.wireOp",EDGE,"E72.1");var subQ16=sQuery(id+"F12.wireOp",EDGE,"E74.1");var subQ18=sQuery(id+"F12.wireOp",EDGE,"E74.8");Q0=qUnion([makeQuery(id+"F12.imprint","IMPRINT",FACE,{"disambiguationData":[TD([[makeQuery(id+"F12.imprint","IMPRINT",EDGE,{"derivedFrom":subQ7}),1.0]])]}),makeQuery(id+"F12.imprint","IMPRINT",FACE,{"disambiguationData":[TD([[makeQuery(id+"F12.imprint","IMPRINT",EDGE,{"derivedFrom":subQ14}),1.0]])]}),makeQuery(id+"F12.imprint","IMPRINT",FACE,{"disambiguationData":[TD([[makeQuery(id+"F12.imprint","IMPRINT",EDGE,{"derivedFrom":subQ16}),1.0]])]}),makeQuery(id+"F12.imprint","IMPRINT",FACE,{"disambiguationData":[TD([[makeQuery(id+"F12.imprint","IMPRINT",EDGE,{"derivedFrom":subQ18}),-1.0]])]})]);}
            var Q1;
            Q1=makeQuery(id+"F5.boolean.opBoolean","SPLIT",FACE,{"disambiguationData":[TD([makeQuery(id+"F5.opExtrude","SWEPT_FACE",FACE,{"disambiguationData":[OSD([sQuery(id+"F4.wireOp",EDGE,"E41")])]})])],"derivedFrom":makeQuery(id+"F3.boolean.opBoolean","COPY",FACE,{"derivedFrom":makeQuery(id+"F3.opExtrude","CAP_FACE",FACE,{"disambiguationData":[OSD([sQuery(id+"F0.wireOp",EDGE,"E25.0"),sQuery(id+"F0.wireOp",EDGE,"E25.1"),sQuery(id+"F0.wireOp",EDGE,"E25.2"),sQuery(id+"F0.wireOp",EDGE,"E25.3"),sQuery(id+"F0.wireOp",EDGE,"E25.4"),sQuery(id+"F0.wireOp",EDGE,"E25.5"),sQuery(id+"F0.wireOp",EDGE,"E25.6"),sQuery(id+"F0.wireOp",EDGE,"E25.7")])],"isStart":false})})});
            extrude(context, id + "F13", {"entities" : qUnion([Q0]), "operationType" : NewBodyOperationType.REMOVE, "endBound" : BoundingType.UP_TO_SURFACE, "endBoundEntityFace" : qUnion([Q1]), "depth" : 25 * mm});
        }
        {
            var Q0;
            Q0=makeQuery(id+"F3.boolean.opBoolean","COPY",EDGE,{"derivedFrom":makeQuery(id+"F3.opExtrude","CAP_EDGE",EDGE,{"disambiguationData":[OSD([sQuery(id+"F0.wireOp",EDGE,"E25.6")])],"isStart":false})});
            var Q1;
            Q1=makeQuery(id+"F8.boolean.opBoolean","INTERSECT",EDGE,{"derivedFrom":[makeQuery(id+"F5.opExtrude","SWEPT_FACE",FACE,{"disambiguationData":[OSD([sQuery(id+"F4.wireOp",EDGE,"E30")])]}),makeQuery(id+"F8.opExtrude","CAP_FACE",FACE,{"disambiguationData":[OSD([sQuery(id+"F7.wireOp",EDGE,"E67")])],"isStart":false})]});
            var Q2;
            Q2=makeQuery(id+"F8.boolean.opBoolean","INTERSECT",EDGE,{"disambiguationData":[OD(1.0)],"derivedFrom":[makeQuery(id+"F5.opExtrude","SWEPT_FACE",FACE,{"disambiguationData":[OSD([sQuery(id+"F4.wireOp",EDGE,"E30")])]}),makeQuery(id+"F8.opExtrude","SWEPT_FACE",FACE,{"disambiguationData":[OSD([sQuery(id+"F7.wireOp",EDGE,"E67")])]})]});
            var Q3;
            {var subQ0=sQuery(id+"F4.wireOp",EDGE,"E30");Q3=makeQuery(id+"F8.boolean.opBoolean","SPLIT",EDGE,{"disambiguationData":[TD([makeQuery(id+"F5.opExtrude","SWEPT_FACE",FACE,{"disambiguationData":[OSD([sQuery(id+"F4.wireOp",EDGE,"E35.filletArc")])]})])],"derivedFrom":makeQuery(id+"F5.opExtrude","CAP_EDGE",EDGE,{"disambiguationData":[OSD([subQ0])],"isStart":false})});}
            var Q4;
            {var subQ0=sQuery(id+"F0.wireOp",EDGE,"E25.7");var subQ1=sQuery(id+"F0.wireOp",EDGE,"E25.1");var subQ2=sQuery(id+"F0.wireOp",EDGE,"E25.6");var subQ3=sQuery(id+"F0.wireOp",EDGE,"E25.5");var subQ4=sQuery(id+"F0.wireOp",EDGE,"E25.4");var subQ5=sQuery(id+"F0.wireOp",EDGE,"E25.0");var subQ6=sQuery(id+"F0.wireOp",EDGE,"E25.2");var subQ7=sQuery(id+"F0.wireOp",EDGE,"E25.3");Q4=makeQuery(id+"F8.boolean.opBoolean","INTERSECT",EDGE,{"derivedFrom":[makeQuery(id+"F5.boolean.opBoolean","SPLIT",FACE,{"disambiguationData":[TD([makeQuery(id+"F2.opExtrude","SWEPT_FACE",FACE,{"disambiguationData":[OSD([subQ5])]})])],"derivedFrom":makeQuery(id+"F3.boolean.opBoolean","COPY",FACE,{"derivedFrom":makeQuery(id+"F3.opExtrude","CAP_FACE",FACE,{"disambiguationData":[OSD([subQ5,subQ1,subQ6,subQ7,subQ4,subQ3,subQ2,subQ0])],"isStart":false})})}),makeQuery(id+"F8.opExtrude","SWEPT_FACE",FACE,{"disambiguationData":[OSD([sQuery(id+"F7.wireOp",EDGE,"E67")])]})]});}
            var Q5;
            Q5=makeQuery(id+"F8.boolean.opBoolean","INTERSECT",EDGE,{"disambiguationData":[OD(0.0)],"derivedFrom":[makeQuery(id+"F5.opExtrude","SWEPT_FACE",FACE,{"disambiguationData":[OSD([sQuery(id+"F4.wireOp",EDGE,"E30")])]}),makeQuery(id+"F8.opExtrude","SWEPT_FACE",FACE,{"disambiguationData":[OSD([sQuery(id+"F7.wireOp",EDGE,"E67")])]})]});
            fillet(context, id + "F14", {"entities" : qUnion([Q0, Q1, Q2, Q3, Q4, Q5]), "radius" : 3 * mm, "tangentPropagation" : true, "allowEdgeOverflow" : false});
        }
        {
            var Q0;
            Q0=makeQuery(id+"F1.opExtrude","CAP_EDGE",EDGE,{"disambiguationData":[OSD([sQuery(id+"F0.wireOp",EDGE,"E1.bottom")])],"isStart":false});
            fillet(context, id + "F15", {"entities" : qUnion([Q0]), "radius" : 2 * mm, "tangentPropagation" : true, "allowEdgeOverflow" : false});
        }
        {
            var Q0;
            {var subQ0=sQuery(id+"F0.wireOp",EDGE,"E21.filletArc");var subQ1=sQuery(id+"F0.wireOp",EDGE,"E7");var subQ2=sQuery(id+"F0.wireOp",EDGE,"E6");var subQ3=sQuery(id+"F0.wireOp",EDGE,"E5");var subQ4=sQuery(id+"F0.wireOp",EDGE,"E4");var subQ5=sQuery(id+"F0.wireOp",EDGE,"E22.filletArc");var subQ6=sQuery(id+"F0.wireOp",EDGE,"E1.bottom");var subQ7=sQuery(id+"F0.wireOp",EDGE,"E1.right");var subQ8=sQuery(id+"F0.wireOp",EDGE,"E1.top");var subQ9=sQuery(id+"F0.wireOp",EDGE,"E1.left");var subQ10=sQuery(id+"F0.wireOp",EDGE,"E23.filletArc");var subQ11=sQuery(id+"F0.wireOp",EDGE,"E24.filletArc");Q0=makeQuery(id+"F2.boolean.opBoolean","SPLIT",FACE,{"disambiguationData":[TD([makeQuery(id+"F1.opExtrude","SWEPT_FACE",FACE,{"disambiguationData":[OSD([subQ6])]})])],"derivedFrom":makeQuery(id+"F1.opExtrude","CAP_FACE",FACE,{"disambiguationData":[OSD([subQ6,subQ8,subQ9,subQ7,subQ4,subQ3,subQ2,subQ1,subQ0,subQ5,subQ10,subQ11])],"isStart":true})});}
            var sketch = newSketch(context, id + "F16", { "sketchPlane" : qUnion([Q0])});
            skLineSegment(sketch, "E79.0", {"start": v(-70, 90) * mm, "end": v(70, 90) * mm});
            skLineSegment(sketch, "E79.1", {"start": v(-80, -80) * mm, "end": v(-80, 80) * mm});
            skCircle(sketch, "E79.2", {"center": v(-60, 67.5) * mm, "radius": 4 * mm});
            skArc(sketch, "E79.3", {"start": v(-70, 90) * mm, "mid": v(-77.07, 87.07) * mm, "end": v(-80, 80) * mm});
            skArc(sketch, "E79.4", {"start": v(80, 80) * mm, "mid": v(77.07, 87.07) * mm, "end": v(70, 90) * mm});
            skLineSegment(sketch, "E79.5", {"start": v(80, -80) * mm, "end": v(80, 80) * mm});
            skCircle(sketch, "E79.6", {"center": v(60, 67.5) * mm, "radius": 4 * mm});
            skArc(sketch, "E79.7", {"start": v(56.15, 48.18) * mm, "mid": v(0, 67.5) * mm, "end": v(-56.15, 48.18) * mm});
            skArc(sketch, "E79.8", {"start": v(60, 40.3) * mm, "mid": v(58.99, 44.68) * mm, "end": v(56.15, 48.18) * mm});
            skLineSegment(sketch, "E79.9", {"start": v(60, 40.3) * mm, "end": v(60, -40.3) * mm});
            skArc(sketch, "E79.10", {"start": v(-56.15, 48.18) * mm, "mid": v(-58.99, 44.68) * mm, "end": v(-60, 40.3) * mm});
            skLineSegment(sketch, "E79.11", {"start": v(-60, 40.3) * mm, "end": v(-60, -40.3) * mm});
            skArc(sketch, "E79.12", {"start": v(-60, -40.3) * mm, "mid": v(-58.99, -44.68) * mm, "end": v(-56.15, -48.18) * mm});
            skArc(sketch, "E79.13", {"start": v(-56.15, -48.18) * mm, "mid": v(0, -67.5) * mm, "end": v(56.15, -48.18) * mm});
            skArc(sketch, "E79.14", {"start": v(56.15, -48.18) * mm, "mid": v(58.99, -44.68) * mm, "end": v(60, -40.3) * mm});
            skArc(sketch, "E79.15", {"start": v(70, -90) * mm, "mid": v(77.07, -87.07) * mm, "end": v(80, -80) * mm});
            skLineSegment(sketch, "E79.16", {"start": v(-70, -90) * mm, "end": v(70, -90) * mm});
            skArc(sketch, "E79.17", {"start": v(-80, -80) * mm, "mid": v(-77.07, -87.07) * mm, "end": v(-70, -90) * mm});
            skCircle(sketch, "E79.18", {"center": v(-60, -67.5) * mm, "radius": 4 * mm});
            skCircle(sketch, "E79.19", {"center": v(60, -67.5) * mm, "radius": 4 * mm});
            skLineSegment(sketch, "E80", {"start": v(0, 90) * mm, "end": v(0, 120) * mm, "construction": true});
            skCircle(sketch, "E81", {"center": v(0, 120) * mm, "radius": 6 * mm});
            skLineSegment(sketch, "E82", {"start": v(-33, 90) * mm, "end": v(-15, 108) * mm});
            skLineSegment(sketch, "E83", {"start": v(-15, 108) * mm, "end": v(-15, 120) * mm});
            skArc(sketch, "E84", {"start": v(-15, 120) * mm, "mid": v(0, 135) * mm, "end": v(15, 120) * mm});
            skLineSegment(sketch, "E85", {"start": v(15, 120) * mm, "end": v(15, 108) * mm});
            skLineSegment(sketch, "E86", {"start": v(15, 108) * mm, "end": v(33, 90) * mm});
            skLineSegment(sketch, "E87", {"start": v(-80, 0) * mm, "end": v(80, 0) * mm, "construction": true});
            skLineSegment(sketch, "E88.MirrorCS", {"start": v(15, -108) * mm, "end": v(33, -90) * mm});
            skLineSegment(sketch, "E89.MirrorCS", {"start": v(15, -120) * mm, "end": v(15, -108) * mm});
            skArc(sketch, "E90.MirrorCS", {"start": v(-15, -120) * mm, "mid": v(0, -135) * mm, "end": v(15, -120) * mm});
            skLineSegment(sketch, "E91.MirrorCS", {"start": v(-15, -108) * mm, "end": v(-15, -120) * mm});
            skLineSegment(sketch, "E92.MirrorCS", {"start": v(-33, -90) * mm, "end": v(-15, -108) * mm});
            skCircle(sketch, "E93.MirrorC", {"center": v(0, -120) * mm, "radius": 6 * mm});
            skLineSegment(sketch, "E94.MirrorCS", {"start": v(0, -90) * mm, "end": v(0, -120) * mm, "construction": true});
            skSolve(sketch);
        }
        {
            var Q0;
            Q0 = qSketchRegion(id + "F16", true);
            var Q1;
            Q1=makeQuery(id+"F2.opExtrude","CAP_FACE",FACE,{"disambiguationData":[OSD([sQuery(id+"F0.wireOp",EDGE,"E12"),sQuery(id+"F0.wireOp",EDGE,"E13"),sQuery(id+"F0.wireOp",EDGE,"E14"),sQuery(id+"F0.wireOp",EDGE,"E15"),sQuery(id+"F0.wireOp",EDGE,"E17.filletArc"),sQuery(id+"F0.wireOp",EDGE,"E18.filletArc"),sQuery(id+"F0.wireOp",EDGE,"E19.filletArc"),sQuery(id+"F0.wireOp",EDGE,"E20.filletArc"),sQuery(id+"F0.wireOp",EDGE,"E25.0"),sQuery(id+"F0.wireOp",EDGE,"E25.1"),sQuery(id+"F0.wireOp",EDGE,"E25.2"),sQuery(id+"F0.wireOp",EDGE,"E25.3"),sQuery(id+"F0.wireOp",EDGE,"E25.4"),sQuery(id+"F0.wireOp",EDGE,"E25.5"),sQuery(id+"F0.wireOp",EDGE,"E25.6"),sQuery(id+"F0.wireOp",EDGE,"E25.7")])],"isStart":false});
            extrude(context, id + "F17", {"entities" : qUnion([Q0]), "endBound" : BoundingType.UP_TO_SURFACE, "endBoundEntityFace" : qUnion([Q1]), "depth" : 25 * mm});
        }
    });
